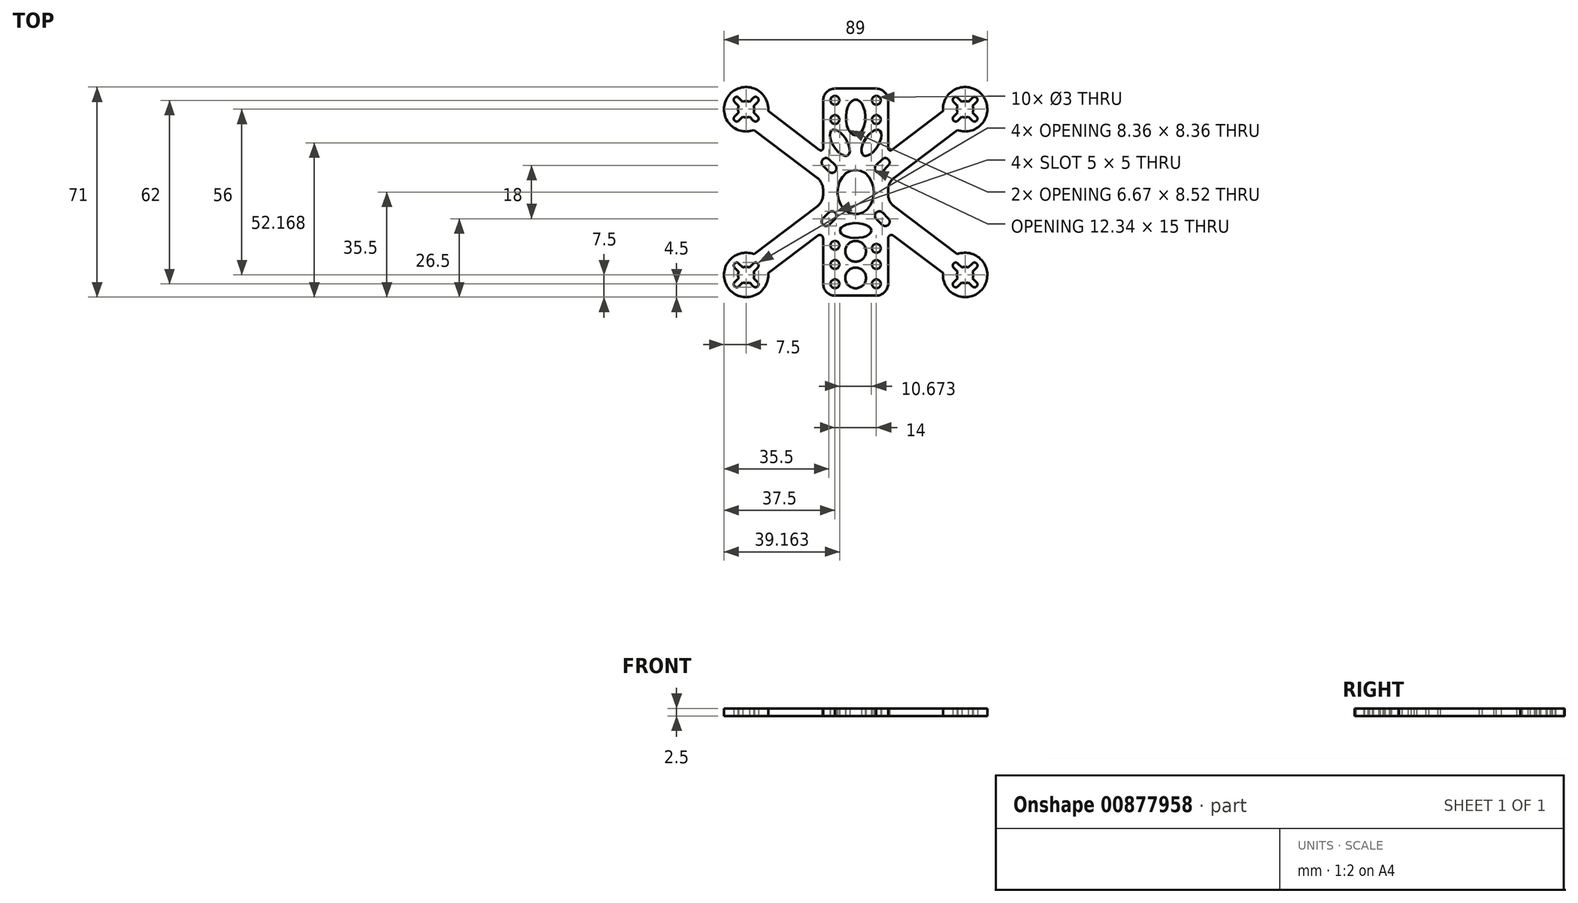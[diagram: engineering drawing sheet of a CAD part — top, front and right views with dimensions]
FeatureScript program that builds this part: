
annotation { "Feature Type Name" : "Feature", "Feature Type Description" : "" }
export const myFeature = defineFeature(function(context is Context, id is Id, definition is map)
    precondition{}
    {
        {
            var Q0;
            Q0=qCreatedBy(makeId("Top.planeOp"),FACE);
            var sketch = newSketch(context, id + "F0", { "sketchPlane" : qUnion([Q0])});
            skPoint(sketch, "E0.middle", {"position": v(0, 0) * mm});
            skCircle(sketch, "E1", {"center": v(37, 28) * mm, "radius": 7.5 * mm});
            skCircle(sketch, "E2.MirrorC", {"center": v(37, -28) * mm, "radius": 7.5 * mm});
            skCircle(sketch, "E3.MirrorC", {"center": v(-37, -28) * mm, "radius": 7.5 * mm});
            skCircle(sketch, "E4.MirrorC", {"center": v(-37, 28) * mm, "radius": 7.5 * mm});
            skCircle(sketch, "E5", {"center": v(-37, 28) * mm, "radius": 2.75 * mm});
            skCircle(sketch, "E6", {"center": v(-33.82, 31.18) * mm, "radius": 1 * mm});
            skLineSegment(sketch, "E7", {"start": v(-34.53, 31.89) * mm, "end": v(-35.9, 30.52) * mm});
            skLineSegment(sketch, "E8", {"start": v(-33.11, 30.47) * mm, "end": v(-34.48, 29.1) * mm});
            skCircle(sketch, "E9.MirrorC", {"center": v(37, 28) * mm, "radius": 2.75 * mm});
            skLineSegment(sketch, "E10.MirrorCS", {"start": v(34.53, 31.89) * mm, "end": v(35.9, 30.52) * mm});
            skCircle(sketch, "E11.MirrorC", {"center": v(33.82, 31.18) * mm, "radius": 1 * mm});
            skLineSegment(sketch, "E12.MirrorCS", {"start": v(33.11, 30.47) * mm, "end": v(34.48, 29.1) * mm});
            skCircle(sketch, "E13.MirrorC", {"center": v(37, -28) * mm, "radius": 2.75 * mm});
            skLineSegment(sketch, "E14.MirrorCS", {"start": v(33.11, -30.47) * mm, "end": v(34.48, -29.1) * mm});
            skCircle(sketch, "E15.MirrorC", {"center": v(33.82, -31.18) * mm, "radius": 1 * mm});
            skLineSegment(sketch, "E16.MirrorCS", {"start": v(34.53, -31.89) * mm, "end": v(35.9, -30.52) * mm});
            skCircle(sketch, "E17.MirrorC", {"center": v(-37, -28) * mm, "radius": 2.75 * mm});
            skLineSegment(sketch, "E18.MirrorCS", {"start": v(-33.11, -30.47) * mm, "end": v(-34.48, -29.1) * mm});
            skCircle(sketch, "E19.MirrorC", {"center": v(-33.82, -31.18) * mm, "radius": 1 * mm});
            skLineSegment(sketch, "E20.MirrorCS", {"start": v(-34.53, -31.89) * mm, "end": v(-35.9, -30.52) * mm});
            skLineSegment(sketch, "E21", {"start": v(12.19, 14.24) * mm, "end": v(29.53, 27.36) * mm});
            skLineSegment(sketch, "E22", {"start": v(12.98, 4.8) * mm, "end": v(34.35, 20.98) * mm});
            skCircle(sketch, "E23.MirrorC", {"center": v(40.18, 31.18) * mm, "radius": 1 * mm});
            skLineSegment(sketch, "E24.MirrorCS", {"start": v(39.47, 31.89) * mm, "end": v(38.1, 30.52) * mm});
            skLineSegment(sketch, "E25.MirrorCS", {"start": v(40.89, 30.47) * mm, "end": v(39.52, 29.1) * mm});
            skLineSegment(sketch, "E26.MirrorCS", {"start": v(40.89, 25.53) * mm, "end": v(39.52, 26.9) * mm});
            skCircle(sketch, "E27.MirrorC", {"center": v(40.18, 24.82) * mm, "radius": 1 * mm});
            skLineSegment(sketch, "E28.MirrorCS", {"start": v(39.47, 24.11) * mm, "end": v(38.1, 25.48) * mm});
            skLineSegment(sketch, "E29.MirrorCS", {"start": v(34.53, 24.11) * mm, "end": v(35.9, 25.48) * mm});
            skLineSegment(sketch, "E30.MirrorCS", {"start": v(33.11, 25.53) * mm, "end": v(34.48, 26.9) * mm});
            skCircle(sketch, "E31.MirrorC", {"center": v(33.82, 24.82) * mm, "radius": 1 * mm});
            skLineSegment(sketch, "E32.MirrorCS", {"start": v(-12.98, 4.8) * mm, "end": v(-34.35, 20.98) * mm});
            skLineSegment(sketch, "E33.MirrorCS", {"start": v(-12.19, 14.24) * mm, "end": v(-29.53, 27.36) * mm});
            skLineSegment(sketch, "E34.MirrorCS", {"start": v(-34.53, 24.11) * mm, "end": v(-35.9, 25.48) * mm});
            skCircle(sketch, "E35.MirrorC", {"center": v(-33.82, 24.82) * mm, "radius": 1 * mm});
            skLineSegment(sketch, "E36.MirrorCS", {"start": v(-33.11, 25.53) * mm, "end": v(-34.48, 26.9) * mm});
            skLineSegment(sketch, "E37.MirrorCS", {"start": v(-39.47, 24.11) * mm, "end": v(-38.1, 25.48) * mm});
            skCircle(sketch, "E38.MirrorC", {"center": v(-40.18, 24.82) * mm, "radius": 1 * mm});
            skLineSegment(sketch, "E39.MirrorCS", {"start": v(-40.89, 25.53) * mm, "end": v(-39.52, 26.9) * mm});
            skLineSegment(sketch, "E40.MirrorCS", {"start": v(-40.89, 30.47) * mm, "end": v(-39.52, 29.1) * mm});
            skCircle(sketch, "E41.MirrorC", {"center": v(-40.18, 31.18) * mm, "radius": 1 * mm});
            skLineSegment(sketch, "E42.MirrorCS", {"start": v(-39.47, 31.89) * mm, "end": v(-38.1, 30.52) * mm});
            skLineSegment(sketch, "E43.MirrorCS", {"start": v(-12.98, -4.8) * mm, "end": v(-34.35, -20.98) * mm});
            skLineSegment(sketch, "E44.MirrorCS", {"start": v(12.98, -4.8) * mm, "end": v(34.35, -20.98) * mm});
            skLineSegment(sketch, "E45.MirrorCS", {"start": v(12.82, -14.72) * mm, "end": v(29.53, -27.36) * mm});
            skLineSegment(sketch, "E46.MirrorCS", {"start": v(-33.11, -25.53) * mm, "end": v(-34.48, -26.9) * mm});
            skCircle(sketch, "E47.MirrorC", {"center": v(-33.82, -24.82) * mm, "radius": 1 * mm});
            skLineSegment(sketch, "E48.MirrorCS", {"start": v(-34.53, -24.11) * mm, "end": v(-35.9, -25.48) * mm});
            skLineSegment(sketch, "E49.MirrorCS", {"start": v(-39.47, -24.11) * mm, "end": v(-38.1, -25.48) * mm});
            skCircle(sketch, "E50.MirrorC", {"center": v(-40.18, -24.82) * mm, "radius": 1 * mm});
            skLineSegment(sketch, "E51.MirrorCS", {"start": v(-40.89, -25.53) * mm, "end": v(-39.52, -26.9) * mm});
            skLineSegment(sketch, "E52.MirrorCS", {"start": v(-40.89, -30.47) * mm, "end": v(-39.52, -29.1) * mm});
            skCircle(sketch, "E53.MirrorC", {"center": v(-40.18, -31.18) * mm, "radius": 1 * mm});
            skLineSegment(sketch, "E54.MirrorCS", {"start": v(-39.47, -31.89) * mm, "end": v(-38.1, -30.52) * mm});
            skLineSegment(sketch, "E55.MirrorCS", {"start": v(40.89, -25.53) * mm, "end": v(39.52, -26.9) * mm});
            skCircle(sketch, "E56.MirrorC", {"center": v(40.18, -24.82) * mm, "radius": 1 * mm});
            skLineSegment(sketch, "E57.MirrorCS", {"start": v(39.47, -24.11) * mm, "end": v(38.1, -25.48) * mm});
            skLineSegment(sketch, "E58.MirrorCS", {"start": v(34.53, -24.11) * mm, "end": v(35.9, -25.48) * mm});
            skCircle(sketch, "E59.MirrorC", {"center": v(33.82, -24.82) * mm, "radius": 1 * mm});
            skLineSegment(sketch, "E60.MirrorCS", {"start": v(33.11, -25.53) * mm, "end": v(34.48, -26.9) * mm});
            skLineSegment(sketch, "E61.MirrorCS", {"start": v(40.89, -30.47) * mm, "end": v(39.52, -29.1) * mm});
            skLineSegment(sketch, "E62.MirrorCS", {"start": v(39.47, -31.89) * mm, "end": v(38.1, -30.52) * mm});
            skCircle(sketch, "E63.MirrorC", {"center": v(40.18, -31.18) * mm, "radius": 1 * mm});
            skCircle(sketch, "E64", {"center": v(-7, 31) * mm, "radius": 1.5 * mm});
            skCircle(sketch, "E65.MirrorC", {"center": v(7, 31) * mm, "radius": 1.5 * mm});
            skCircle(sketch, "E66.MirrorC", {"center": v(-7, -31) * mm, "radius": 1.5 * mm});
            skCircle(sketch, "E67.MirrorC", {"center": v(7, -31) * mm, "radius": 1.5 * mm});
            skCircle(sketch, "E68", {"center": v(-8, 8) * mm, "radius": 1.5 * mm});
            skCircle(sketch, "E69.MirrorC", {"center": v(8, 8) * mm, "radius": 1.5 * mm});
            skCircle(sketch, "E70", {"center": v(-8, -8) * mm, "radius": 1.5 * mm});
            skCircle(sketch, "E71", {"center": v(8, -8) * mm, "radius": 1.5 * mm});
            skCircle(sketch, "E72.MirrorC", {"center": v(-7, 24.5) * mm, "radius": 1.5 * mm});
            skCircle(sketch, "E73.MirrorC", {"center": v(7, 24.5) * mm, "radius": 1.5 * mm});
            skArc(sketch, "E74", {"start": v(-7, 35) * mm, "mid": v(-9.78, 33.78) * mm, "end": v(-11, 31) * mm});
            skArc(sketch, "E75.MirrorCS", {"start": v(7, 35) * mm, "mid": v(9.78, 33.78) * mm, "end": v(11, 31) * mm});
            skCircle(sketch, "E76.MirrorC", {"center": v(-7, -24.5) * mm, "radius": 1.5 * mm});
            skCircle(sketch, "E77.MirrorC", {"center": v(7, -24.5) * mm, "radius": 1.5 * mm});
            skArc(sketch, "E78.MirrorCS", {"start": v(7, -35) * mm, "mid": v(9.78, -33.78) * mm, "end": v(11, -31) * mm});
            skArc(sketch, "E79.MirrorCS", {"start": v(-7, -35) * mm, "mid": v(-9.78, -33.78) * mm, "end": v(-11, -31) * mm});
            skLineSegment(sketch, "E80", {"start": v(-7, 35) * mm, "end": v(7, 35) * mm});
            skLineSegment(sketch, "E81", {"start": v(-11, 0.82) * mm, "end": v(-11, -0.82) * mm});
            skLineSegment(sketch, "E82", {"start": v(11, -0.82) * mm, "end": v(11, 0.82) * mm});
            skLineSegment(sketch, "E83", {"start": v(-7, -35) * mm, "end": v(7, -35) * mm});
            skCircle(sketch, "E84.MirrorC", {"center": v(-7, -18) * mm, "radius": 1.5 * mm});
            skCircle(sketch, "E85.MirrorC", {"center": v(7, -19) * mm, "radius": 1.5 * mm});
            skPoint(sketch, "E86", {"position": v(0, -4.13) * mm});
            skPoint(sketch, "E87", {"position": v(0, 30.82) * mm});
            skPoint(sketch, "E88", {"position": v(0, 19.17) * mm});
            skPoint(sketch, "E89", {"position": v(0, -31) * mm});
            skPoint(sketch, "E90.middle", {"position": v(0, -9.01) * mm});
            skPoint(sketch, "E91", {"position": v(0, -11.87) * mm});
            skPoint(sketch, "E92", {"position": v(0, -28.6) * mm});
            skEllipse(sketch, "E93", {"center": v(0, 0) * mm, "majorRadius": 6.17 * mm, "minorRadius": 7.5 * mm, "majorAxis": v(1, 0)});
            skCircle(sketch, "E94", {"center": v(0, -20) * mm, "radius": 3.5 * mm});
            skCircle(sketch, "E95.MirrorC", {"center": v(0, -29) * mm, "radius": 3.5 * mm});
            skEllipse(sketch, "E96", {"center": v(-5.34, 16.67) * mm, "majorRadius": 5.04 * mm, "minorRadius": 2.4 * mm, "majorAxis": v(0.53, -0.85)});
            skEllipse(sketch, "E97.MirrorC", {"center": v(5.34, 16.67) * mm, "majorRadius": 5.04 * mm, "minorRadius": 2.4 * mm, "majorAxis": v(-0.53, -0.85)});
            skEllipse(sketch, "E98", {"center": v(0, -13) * mm, "majorRadius": 5.35 * mm, "minorRadius": 2.5 * mm, "majorAxis": v(1, 0)});
            skEllipse(sketch, "E99", {"center": v(0, 25.22) * mm, "majorRadius": 6.04 * mm, "minorRadius": 3.29 * mm, "majorAxis": v(0, -1)});
            skPoint(sketch, "E100.newPointA", {"position": v(-11, 3.3) * mm});
            skArc(sketch, "E100.filletArc", {"start": v(-11, 0.82) * mm, "mid": v(-11.52, 3.05) * mm, "end": v(-12.98, 4.8) * mm});
            skPoint(sketch, "E101.newPointA", {"position": v(11, 3.3) * mm});
            skArc(sketch, "E101.filletArc", {"start": v(12.98, 4.8) * mm, "mid": v(11.52, 3.05) * mm, "end": v(11, 0.82) * mm});
            skPoint(sketch, "E102.newPointA", {"position": v(11, -3.3) * mm});
            skArc(sketch, "E102.filletArc", {"start": v(11, -0.82) * mm, "mid": v(11.52, -3.05) * mm, "end": v(12.98, -4.8) * mm});
            skPoint(sketch, "E103.newPointA", {"position": v(-11, -3.3) * mm});
            skArc(sketch, "E103.filletArc", {"start": v(-12.98, -4.8) * mm, "mid": v(-11.52, -3.05) * mm, "end": v(-11, -0.82) * mm});
            skLineSegment(sketch, "E104", {"start": v(-11, 15.39) * mm, "end": v(-11, 14.83) * mm});
            skLineSegment(sketch, "E105", {"start": v(11, 15.39) * mm, "end": v(11, 14.83) * mm});
            skLineSegment(sketch, "E106", {"start": v(-11, 31) * mm, "end": v(-11, 15.39) * mm});
            skLineSegment(sketch, "E107", {"start": v(11, 31) * mm, "end": v(11, 15.39) * mm});
            skLineSegment(sketch, "E108", {"start": v(-11, -16.92) * mm, "end": v(-11, -31) * mm});
            skLineSegment(sketch, "E109", {"start": v(11, -15.63) * mm, "end": v(11, -16.92) * mm});
            skLineSegment(sketch, "E110", {"start": v(11, -16.92) * mm, "end": v(11, -31) * mm});
            skPoint(sketch, "E111.visualSharp", {"position": v(11, -13.34) * mm});
            skArc(sketch, "E111.filletArc", {"start": v(12.82, -14.72) * mm, "mid": v(11.63, -14.6) * mm, "end": v(11, -15.63) * mm});
            skArc(sketch, "E112.MirrorCS", {"start": v(-12.82, -14.72) * mm, "mid": v(-11.63, -14.6) * mm, "end": v(-11, -15.63) * mm});
            skLineSegment(sketch, "E113.MirrorCS", {"start": v(-12.82, -14.72) * mm, "end": v(-29.53, -27.36) * mm});
            skLineSegment(sketch, "E114.MirrorCS", {"start": v(-11, -15.63) * mm, "end": v(-11, -16.92) * mm});
            skPoint(sketch, "E115.visualSharp", {"position": v(-11, 13.34) * mm});
            skArc(sketch, "E115.filletArc", {"start": v(-12.19, 14.24) * mm, "mid": v(-11.41, 14.17) * mm, "end": v(-11, 14.83) * mm});
            skPoint(sketch, "E116.visualSharp", {"position": v(11, 13.34) * mm});
            skArc(sketch, "E116.filletArc", {"start": v(11, 14.83) * mm, "mid": v(11.41, 14.17) * mm, "end": v(12.19, 14.24) * mm});
            skCircle(sketch, "E117", {"center": v(-10, 10) * mm, "radius": 1.5 * mm});
            skLineSegment(sketch, "E118", {"start": v(-6.94, 9.06) * mm, "end": v(-8.94, 11.06) * mm});
            skLineSegment(sketch, "E119.MirrorCS", {"start": v(-9.06, 6.94) * mm, "end": v(-11.06, 8.94) * mm});
            skCircle(sketch, "E120.MirrorC", {"center": v(10, 10) * mm, "radius": 1.5 * mm});
            skLineSegment(sketch, "E121.MirrorCS", {"start": v(6.94, 9.06) * mm, "end": v(8.94, 11.06) * mm});
            skLineSegment(sketch, "E122.MirrorCS", {"start": v(9.06, 6.94) * mm, "end": v(11.06, 8.94) * mm});
            skLineSegment(sketch, "E123.MirrorCS", {"start": v(9.06, -6.94) * mm, "end": v(11.06, -8.94) * mm});
            skCircle(sketch, "E124.MirrorC", {"center": v(10, -10) * mm, "radius": 1.5 * mm});
            skLineSegment(sketch, "E125.MirrorCS", {"start": v(6.94, -9.06) * mm, "end": v(8.94, -11.06) * mm});
            skLineSegment(sketch, "E126.MirrorCS", {"start": v(-6.94, -9.06) * mm, "end": v(-8.94, -11.06) * mm});
            skCircle(sketch, "E127.MirrorC", {"center": v(-10, -10) * mm, "radius": 1.5 * mm});
            skLineSegment(sketch, "E128.MirrorCS", {"start": v(-9.06, -6.94) * mm, "end": v(-11.06, -8.94) * mm});
            skSolve(sketch);
        }
        {
            var Q0;
            Q0=qSketchRegion(id+"F0",true);
            extrude(context, id + "F1", {"entities" : qUnion([Q0]), "depth" : 2.5 * mm, "offsetDistance" : 25 * mm});
        }
    });
